# Revit family: Sanitary_Toilet-Seats_Sanindusa_Look-Toilet-Seat-And-Cover-With-Clipoff-And-Slowclose-System
name_source: partatom
category: Plumbing Fixtures
revit_build: Autodesk Revit 2018 (Build: 20170223_1515(x64)
units: mm (PartAtom-declared; Revit-internal decimal feet)

## family parameters
Always vertical = Yes
Cut with Voids When Loaded = No
OmniClass Number = 23.45.00.00
OmniClass Title = Sanitary, Laundry, and Cleaning Equipment
Part Type = Normal
Room Calculation Point = No
Round Connector Dimension = Use Diameter
Shared = No
Work Plane-Based = No

## types (1)
- Sanitary_Toilet-Seats_Sanindusa_Look-Toilet-Seat-And-Cover-With-Clipoff-And-Slowclose-System
    AssetType = Fixed
    CartridgeType = D35 mm open ceramic cartridge
    Color = white
    Constituents = 2341111-fixing kit for toilet seat (included)
    Cost = 0 $
    Description = toilet seat and cover
    Edition number = 1
    Element Type = WCSEAT: Hinged seat that fits on the top of a water closet (WC) pan. (BS6100 330 1401)
    Features = Duroplast is a material that does not contain substances hazardous to the environment and therefore is compatible with the skin, is anti-bacterial, antistatic, dust repellent and resistant to fading under UV rays. This toilet seat and cover also has a slow close system, to prevent abrupt drops and it has a clipoff system that allows you to remove the lid and the seat for an easy cleaning.
    Finish = gloss
    FlowRateMaximum = 17 L/min at 3 bar
    InletConnectionType = 2 x M10x1-3/8 stainless steel flexible supply hoses
    Installation Instructions = https://www.tec.sanindusa.pt
    InstallationDate = 1900-12-31T23:59:59
    Manufacturer = Sanindusa
    ManufacturerName = Sanindusa
    ManufacturerURL = www.tec.sanindusa.pt
    Material = Duroplast
    ModelNumber = 2343100
    ModelReference = Look
    Name = Look toilet seat and cover with clipoff and slowclose system
    NominalHeight = 39 mm  [stored 0.127953 ft]
    NominalLength = 344 mm  [stored 1.12861 ft]
    NominalWidth = 442 mm  [stored 1.45013 ft]
    Pre-defined type (IFC) = WCSEAT
    Product Guid = 85b9b0e3-691c-4632-ad41-6304badbafbb
    Product data url = https://bimobject.com
    ProductInformation = https://www.tec.sanindusa.pt
    ProductionYear = 2017
    Size = 34x44
    Type (IFC) = IfcSanitaryTerminalType
    URL = www.tec.sanindusa.pt
    Uniclass2015Code = Pr_40_20_93_95
    Uniclass2015Title = WC seats and covers
    Uniclass2015Version = Products v1.6
    Version = 2
    WarrantyDescription = https://www.tec.sanindusa.pt
    WarrantyDurationParts = v
    WarrantyDurationUnit = year
    WarrantyStartDate = 1900-12-31T23:59:59
1900-12-31T23:59:59
    Weight = 2.70 kg

note: [stored X ft] marks values corroborated as IEEE doubles in the binary element streams (Revit-internal decimal feet)

## geometry (parser evidence)
native form markers: Sweep x7
no freeform markers — native parametric forms only
